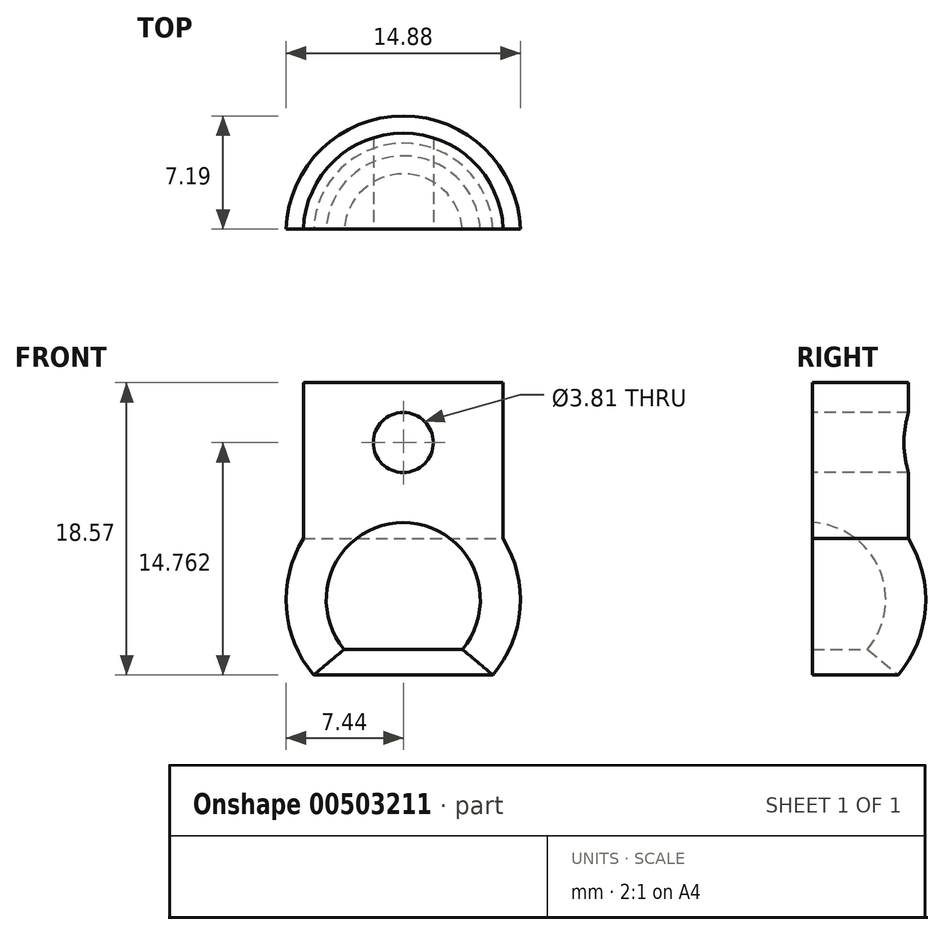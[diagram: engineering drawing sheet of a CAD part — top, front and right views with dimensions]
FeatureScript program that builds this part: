
annotation { "Feature Type Name" : "Feature", "Feature Type Description" : "" }
export const myFeature = defineFeature(function(context is Context, id is Id, definition is map)
    precondition{}
    {
        {
            var Q0;
            Q0=qCreatedBy(makeId("Front.planeOp"),FACE);
            var sketch = newSketch(context, id + "F0", { "sketchPlane" : qUnion([Q0])});
            skArc(sketch, "E0", {"start": v(3.76, -3.15) * mm, "mid": v(4.44, 2.07) * mm, "end": v(0, 4.9) * mm});
            skArc(sketch, "E1.0", {"start": v(5.7, -4.78) * mm, "mid": v(7.42, -0.56) * mm, "end": v(6.35, 3.88) * mm});
            skLineSegment(sketch, "E2", {"start": v(0, 4.9) * mm, "end": v(0, 7.44) * mm});
            skLineSegment(sketch, "E3.top", {"start": v(0, 13.8) * mm, "end": v(6.35, 13.8) * mm});
            skLineSegment(sketch, "E3.left", {"start": v(0, 7.44) * mm, "end": v(0, 13.8) * mm});
            skLineSegment(sketch, "E3.right", {"start": v(6.35, 7.3) * mm, "end": v(6.35, 13.8) * mm});
            skLineSegment(sketch, "E4", {"start": v(6.35, 7.3) * mm, "end": v(6.35, 3.88) * mm});
            skLineSegment(sketch, "E5", {"start": v(3.76, -3.15) * mm, "end": v(5.7, -4.78) * mm});
            skSolve(sketch);
        }
        {
            var Q0;
            Q0=makeQuery(id+"F0.imprint","IMPRINT",FACE,{"disambiguationData":[TD([[makeQuery(id+"F0.imprint","IMPRINT",EDGE,{"derivedFrom":sQuery(id+"F0.wireOp",EDGE,"E0")}),-1.0]])]});
            var Q1;
            Q1=sQuery(id+"F0.wireOp",EDGE,"E3.left");
            revolve(context, id + "F1", {"entities" : qUnion([Q0]), "axis" : qUnion([Q1]), "revolveType" : RevolveType.ONE_DIRECTION, "angle" : 180 * degree});
        }
        {
            var Q0;
            Q0=makeQuery(id+"F1.opRevolve","CAP_FACE",FACE,{"disambiguationData":[OSD([sQuery(id+"F0.wireOp",EDGE,"E0"),sQuery(id+"F0.wireOp",EDGE,"E1.0"),sQuery(id+"F0.wireOp",EDGE,"E2"),sQuery(id+"F0.wireOp",EDGE,"E3.top"),sQuery(id+"F0.wireOp",EDGE,"E3.left"),sQuery(id+"F0.wireOp",EDGE,"E3.right"),sQuery(id+"F0.wireOp",EDGE,"E4"),sQuery(id+"F0.wireOp",EDGE,"E5")])],"isStart":true});
            var sketch = newSketch(context, id + "F2", { "sketchPlane" : qUnion([Q0])});
            skSolve(sketch);
        }
        {
            var Q0;
            Q0=makeQuery(id+"F2.imprint","IMPRINT",FACE,{"disambiguationData":[TD([[makeQuery(id+"F2.imprint","IMPRINT",EDGE,{"derivedFrom":makeQuery(id+"F1.opRevolve","CAP_EDGE",EDGE,{"disambiguationData":[OSD([sQuery(id+"F0.wireOp",EDGE,"E0")])],"isStart":true})}),1.0]])]});
            var sketch = newSketch(context, id + "F3", { "sketchPlane" : qUnion([Q0])});
            skCircle(sketch, "E6", {"center": v(0, 9.98) * mm, "radius": 1.9 * mm});
            skSolve(sketch);
        }
        {
            var Q0;
            Q0=makeQuery(id+"F3.imprint","IMPRINT",FACE,{"disambiguationData":[TD([[makeQuery(id+"F3.imprint","IMPRINT",EDGE,{"derivedFrom":sQuery(id+"F3.wireOp",EDGE,"E6")}),1.0]])]});
            extrude(context, id + "F4", {"entities" : qUnion([Q0]), "operationType" : NewBodyOperationType.REMOVE, "endBound" : BoundingType.THROUGH_ALL, "oppositeDirection" : true, "depth" : 25.4 * mm});
        }
        {
            var Q0;
            Q0=makeQuery(id+"F1.opRevolve","SWEPT_FACE",FACE,{"disambiguationData":[OSD([sQuery(id+"F0.wireOp",EDGE,"E3.top")])]});
            var sketch = newSketch(context, id + "F5", { "sketchPlane" : qUnion([Q0])});
            skLineSegment(sketch, "E7.bottom", {"start": v(-9.53, 0) * mm, "end": v(9.53, 0) * mm});
            skLineSegment(sketch, "E7.top", {"start": v(-9.53, 0.25) * mm, "end": v(9.53, 0.25) * mm});
            skLineSegment(sketch, "E7.left", {"start": v(-9.53, 0) * mm, "end": v(-9.53, 0.25) * mm});
            skLineSegment(sketch, "E7.right", {"start": v(9.53, 0) * mm, "end": v(9.53, 0.25) * mm});
            skSolve(sketch);
        }
        {
            var Q0;
            {var subQ0=sQuery(id+"F5.wireOp",EDGE,"E7.bottom");var subQ1=makeQuery(id+"F1.opRevolve","SWEPT_EDGE",EDGE,{"disambiguationData":[OSD([sQuery(id+"F0.wireOp",EDGE,"E3.top"),sQuery(id+"F0.wireOp",EDGE,"E3.right")])]});var subQ2=makeQuery(id+"F5.imprint","INTERSECT",VERTEX,{"disambiguationData":[OD(0.0)],"derivedFrom":[subQ1,subQ0]});var subQ3=makeQuery(id+"F5.imprint","INTERSECT",VERTEX,{"disambiguationData":[OD(1.0)],"derivedFrom":[subQ1,subQ0]});Q0=makeQuery(id+"F5.imprint","IMPRINT",FACE,{"disambiguationData":[TD([[makeQuery(id+"F5.imprint","IMPRINT",EDGE,{"disambiguationData":[TD([[subQ2,-1.0],[subQ3,1.0]])],"derivedFrom":subQ0}),-1.0]])]});}
            var Q1;
            {var subQ3=sQuery(id+"F5.wireOp",EDGE,"E7.left");Q1=makeQuery(id+"F5.imprint","IMPRINT",FACE,{"disambiguationData":[TD([[makeQuery(id+"F5.imprint","IMPRINT",EDGE,{"derivedFrom":subQ3}),-1.0]])]});}
            var Q2;
            {var subQ3=sQuery(id+"F5.wireOp",EDGE,"E7.right");Q2=makeQuery(id+"F5.imprint","IMPRINT",FACE,{"disambiguationData":[TD([[makeQuery(id+"F5.imprint","IMPRINT",EDGE,{"derivedFrom":subQ3}),1.0]])]});}
            extrude(context, id + "F6", {"entities" : qUnion([Q0, Q1, Q2]), "operationType" : NewBodyOperationType.REMOVE, "endBound" : BoundingType.THROUGH_ALL, "oppositeDirection" : true, "depth" : 25.4 * mm});
        }
    });
